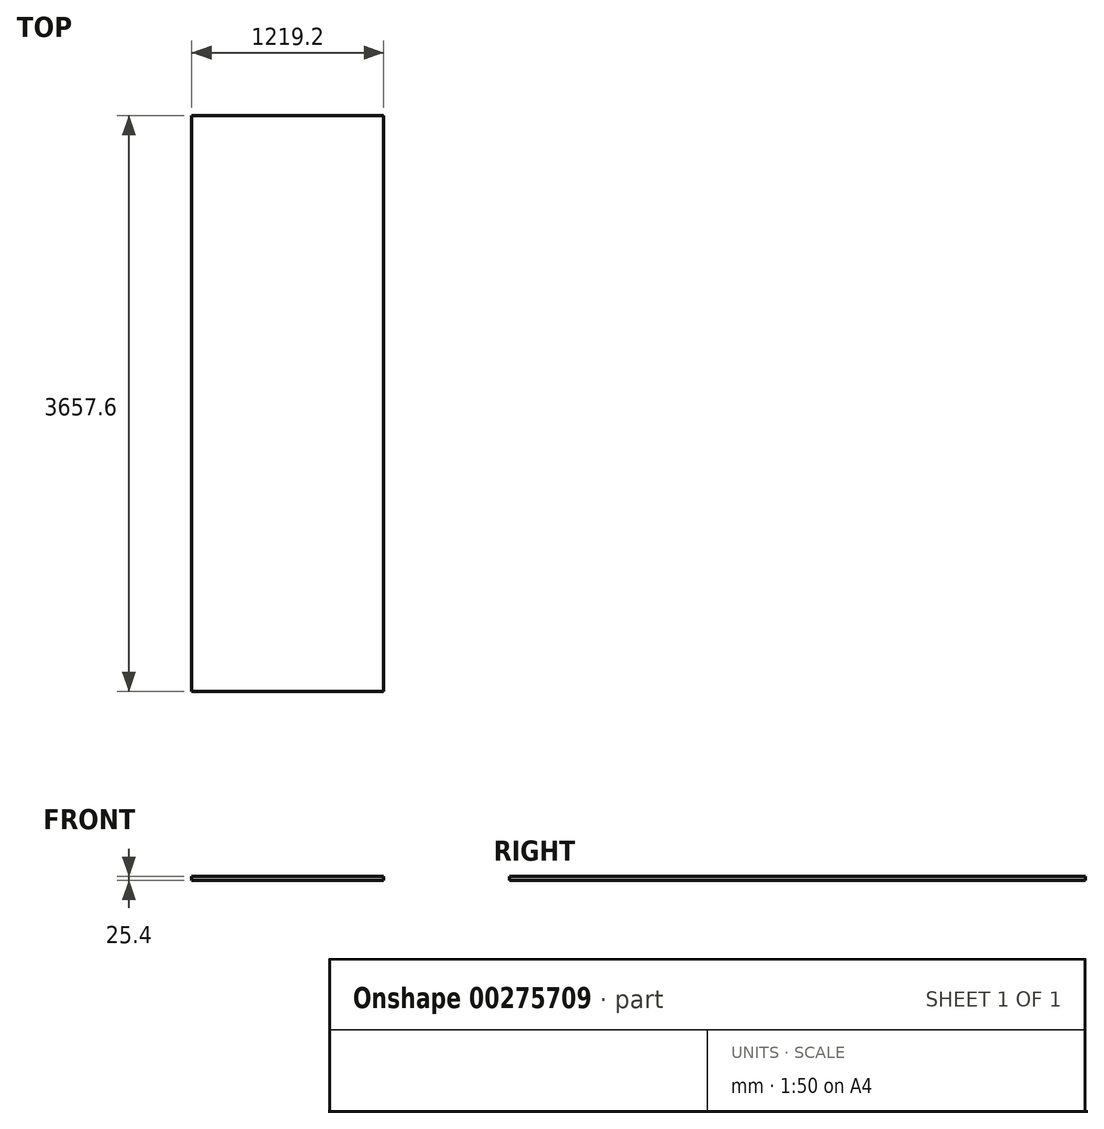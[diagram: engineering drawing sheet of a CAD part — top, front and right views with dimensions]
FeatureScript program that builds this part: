
annotation { "Feature Type Name" : "Feature", "Feature Type Description" : "" }
export const myFeature = defineFeature(function(context is Context, id is Id, definition is map)
    precondition{}
    {
        {
            var Q0;
            Q0=qCreatedBy(makeId("Top.planeOp"),FACE);
            var sketch = newSketch(context, id + "F0", { "sketchPlane" : qUnion([Q0])});
            skLineSegment(sketch, "E0.bottom", {"start": v(0, 0) * mm, "end": v(1219.2, 0) * mm});
            skLineSegment(sketch, "E0.top", {"start": v(0, 3657.6) * mm, "end": v(1219.2, 3657.6) * mm});
            skLineSegment(sketch, "E0.left", {"start": v(0, 0) * mm, "end": v(0, 3657.6) * mm});
            skLineSegment(sketch, "E0.right", {"start": v(1219.2, 0) * mm, "end": v(1219.2, 3657.6) * mm});
            skSolve(sketch);
        }
        {
            var Q0;
            Q0=makeQuery(id+"F0.imprint","IMPRINT",FACE,{"disambiguationData":[TD([[makeQuery(id+"F0.imprint","IMPRINT",EDGE,{"derivedFrom":sQuery(id+"F0.wireOp",EDGE,"E0.bottom")}),1.0]])]});
            extrude(context, id + "F1", {"entities" : qUnion([Q0]), "depth" : 25.4 * mm, "offsetDistance" : 25.4 * mm});
        }
    });
